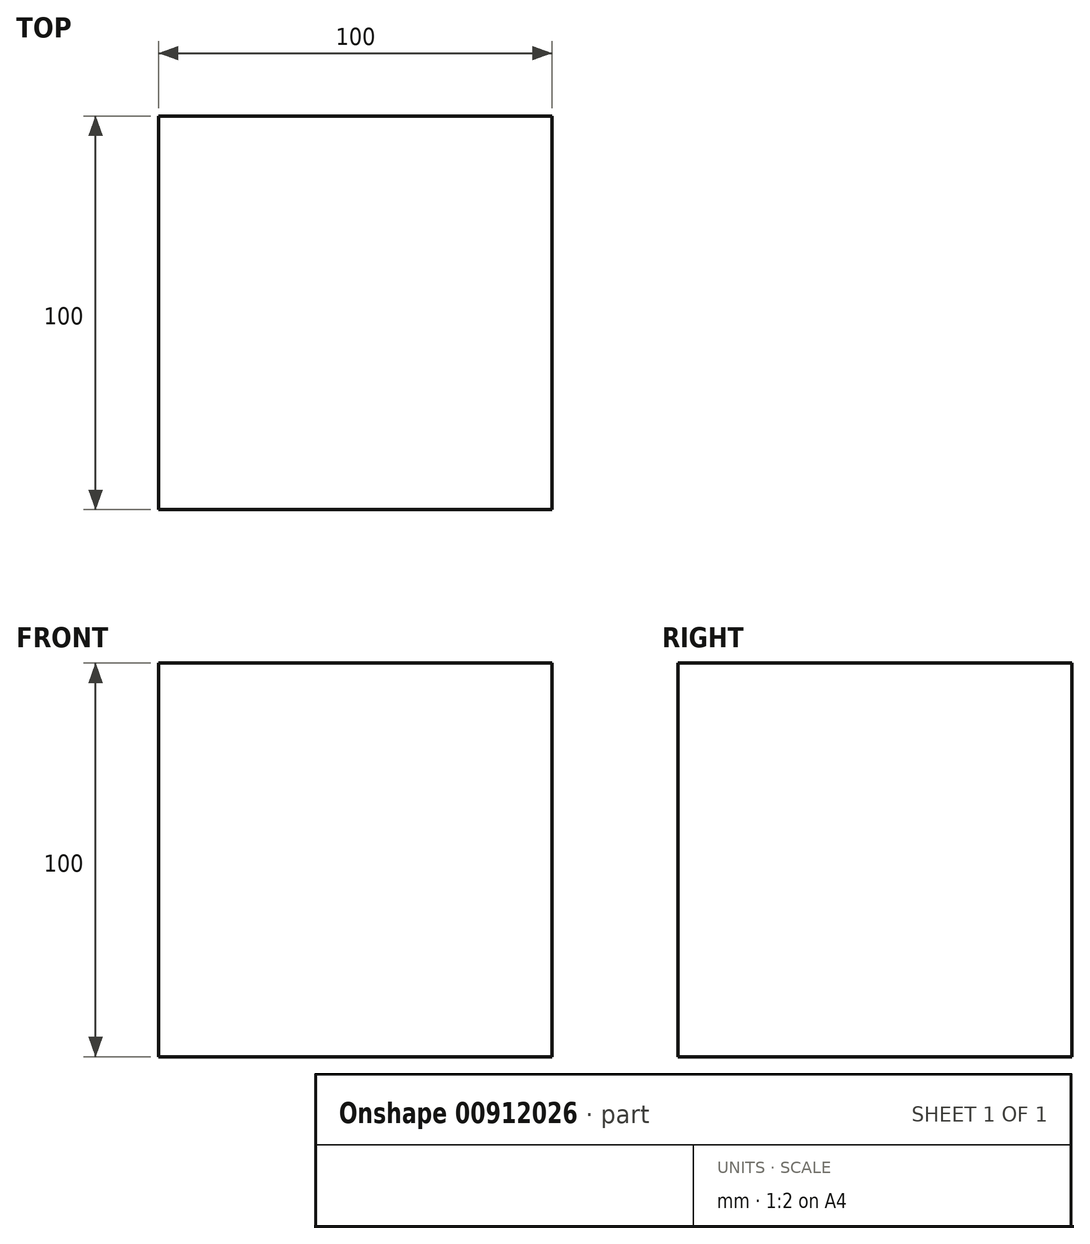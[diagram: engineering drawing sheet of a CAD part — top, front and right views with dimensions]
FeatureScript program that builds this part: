
annotation { "Feature Type Name" : "Feature", "Feature Type Description" : "" }
export const myFeature = defineFeature(function(context is Context, id is Id, definition is map)
    precondition{}
    {
        {
            var Q0;
            Q0=qCreatedBy(makeId("Top.planeOp"),FACE);
            var sketch = newSketch(context, id + "F0", { "sketchPlane" : qUnion([Q0])});
            skCircle(sketch, "E0.cCircle", {"center": v(0, 0) * mm, "radius": 50 * mm, "construction": true});
            skLineSegment(sketch, "E0.0", {"start": v(50, 50) * mm, "end": v(50, -50) * mm});
            skLineSegment(sketch, "E0.1", {"start": v(50, -50) * mm, "end": v(-50, -50) * mm});
            skLineSegment(sketch, "E0.2", {"start": v(-50, -50) * mm, "end": v(-50, 50) * mm});
            skLineSegment(sketch, "E0.3", {"start": v(-50, 50) * mm, "end": v(50, 50) * mm});
            skPoint(sketch, "E0.0.midPoint", {"position": v(50, 0) * mm});
            skSolve(sketch);
        }
        {
            var Q0;
            Q0=makeQuery(id+"F0.imprint","IMPRINT",FACE,{"disambiguationData":[TD([[makeQuery(id+"F0.imprint","IMPRINT",EDGE,{"derivedFrom":sQuery(id+"F0.wireOp",EDGE,"E0.0")}),-1.0]])]});
            extrude(context, id + "F1", {"entities" : qUnion([Q0]), "depth" : 100 * mm, "offsetDistance" : 25 * mm});
        }
    });
